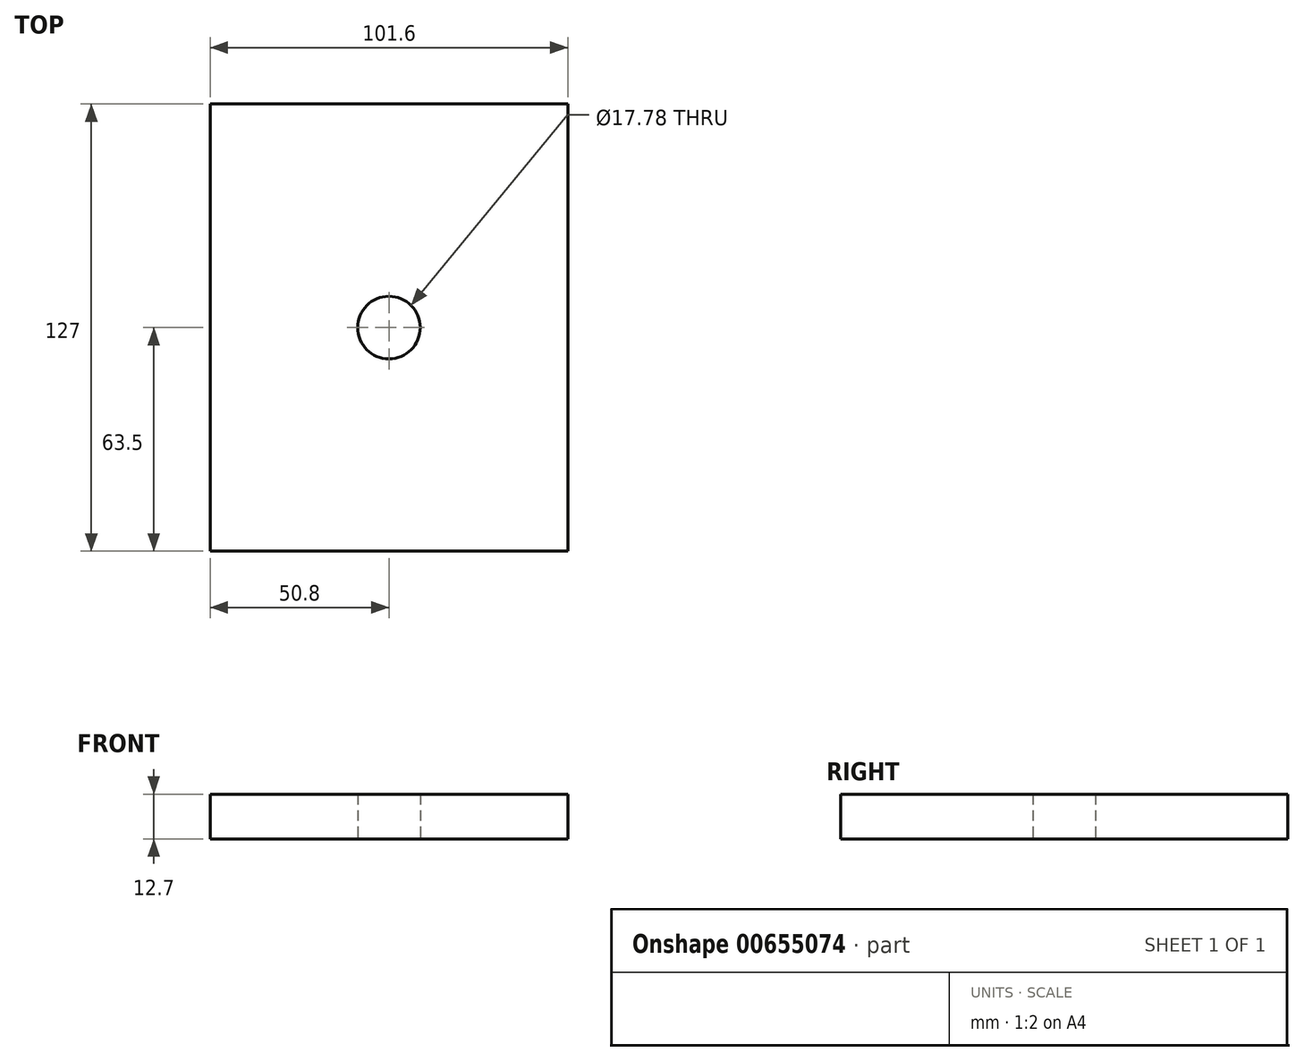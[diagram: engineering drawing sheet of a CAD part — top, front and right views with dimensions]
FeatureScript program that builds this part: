
annotation { "Feature Type Name" : "Feature", "Feature Type Description" : "" }
export const myFeature = defineFeature(function(context is Context, id is Id, definition is map)
    precondition{}
    {
        {
            var Q0;
            Q0=qCreatedBy(makeId("Top.planeOp"),FACE);
            var sketch = newSketch(context, id + "F0", { "sketchPlane" : qUnion([Q0])});
            skLineSegment(sketch, "E0.bottom", {"start": v(-50.8, 63.5) * mm, "end": v(50.8, 63.5) * mm});
            skLineSegment(sketch, "E0.top", {"start": v(-50.8, -63.5) * mm, "end": v(50.8, -63.5) * mm});
            skLineSegment(sketch, "E0.left", {"start": v(-50.8, 63.5) * mm, "end": v(-50.8, -63.5) * mm});
            skLineSegment(sketch, "E0.right", {"start": v(50.8, 63.5) * mm, "end": v(50.8, -63.5) * mm});
            skPoint(sketch, "E0.middle", {"position": v(0, 0) * mm});
            skCircle(sketch, "E1", {"center": v(0, 0) * mm, "radius": 8.9 * mm});
            skSolve(sketch);
        }
        {
            var Q0;
            Q0=makeQuery(id+"F0.imprint","IMPRINT",FACE,{"disambiguationData":[TD([[makeQuery(id+"F0.imprint","IMPRINT",EDGE,{"derivedFrom":sQuery(id+"F0.wireOp",EDGE,"E0.bottom")}),-1.0]])]});
            extrude(context, id + "F1", {"entities" : qUnion([Q0]), "depth" : 12.7 * mm, "offsetDistance" : 25.4 * mm});
        }
    });
